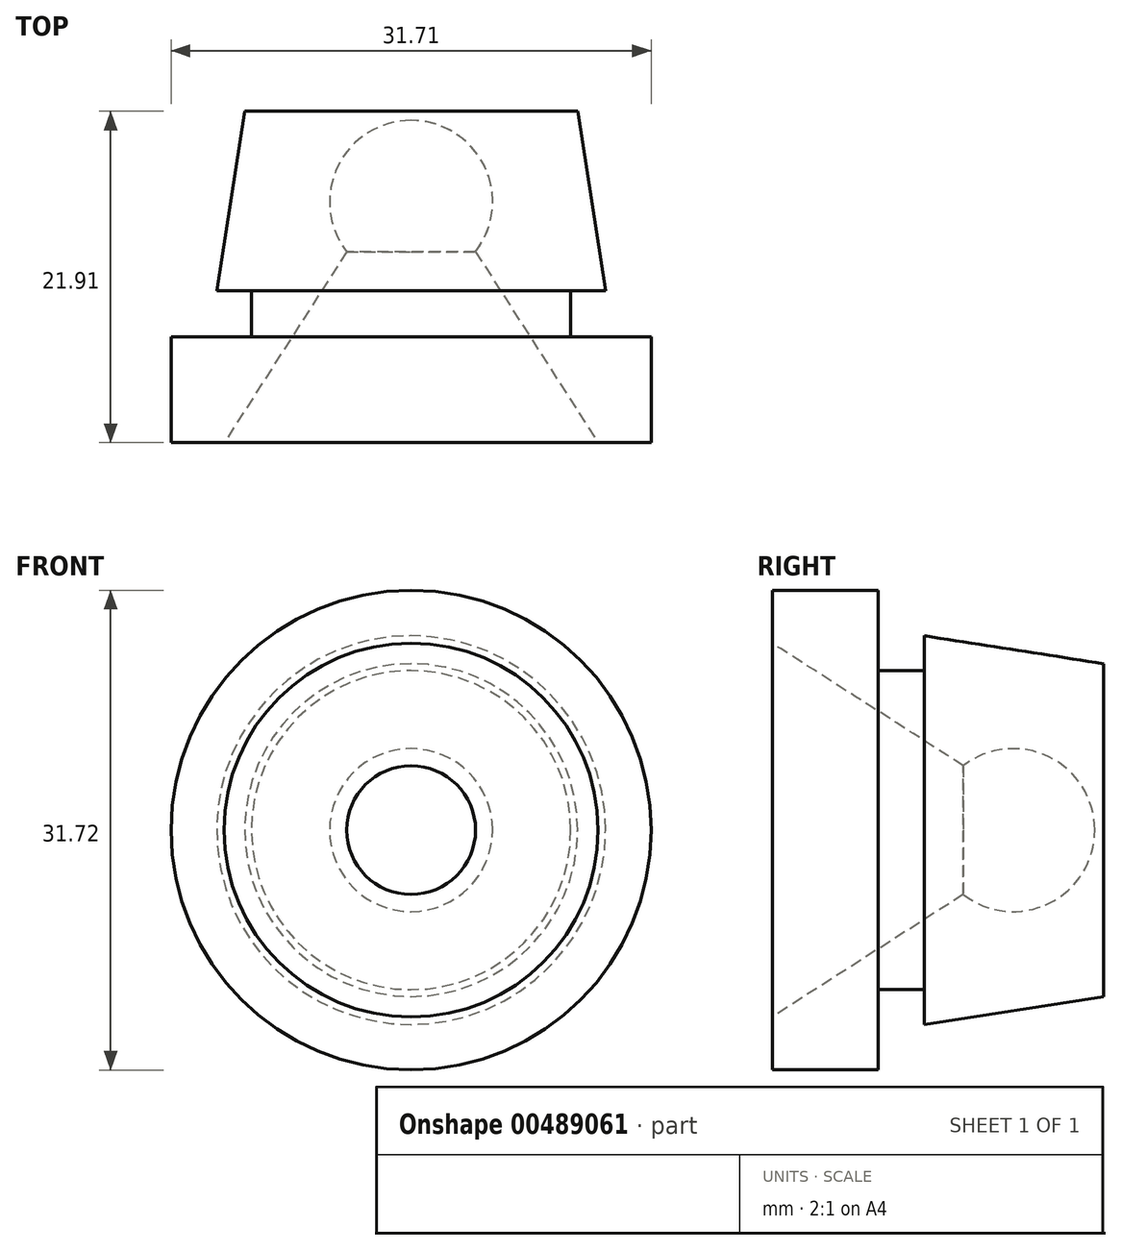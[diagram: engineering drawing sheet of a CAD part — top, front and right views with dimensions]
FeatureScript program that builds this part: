
annotation { "Feature Type Name" : "Feature", "Feature Type Description" : "" }
export const myFeature = defineFeature(function(context is Context, id is Id, definition is map)
    precondition{}
    {
        {
            var Q0;
            Q0=qCreatedBy(makeId("Top.planeOp"),FACE);
            var sketch = newSketch(context, id + "F0", { "sketchPlane" : qUnion([Q0])});
            skLineSegment(sketch, "E0", {"start": v(0, 0) * mm, "end": v(3.5, 0) * mm});
            skLineSegment(sketch, "E1", {"start": v(3.5, 0) * mm, "end": v(3.5, 7) * mm});
            skLineSegment(sketch, "E2", {"start": v(3.5, 7) * mm, "end": v(-1.81, 7) * mm});
            skLineSegment(sketch, "E3", {"start": v(-1.81, 7) * mm, "end": v(-1.81, 10.05) * mm});
            skLineSegment(sketch, "E4", {"start": v(-1.81, 10.05) * mm, "end": v(0.5, 10.05) * mm});
            skLineSegment(sketch, "E5", {"start": v(0.5, 10.05) * mm, "end": v(-1.36, 21.9) * mm});
            skLineSegment(sketch, "E6", {"start": v(-1.36, 21.9) * mm, "end": v(-12.36, 21.9) * mm});
            skLineSegment(sketch, "E7", {"start": v(0, 0) * mm, "end": v(-8.1, 12.62) * mm});
            skArc(sketch, "E8", {"start": v(-8.1, 12.62) * mm, "mid": v(-7.52, 18.3) * mm, "end": v(-12.36, 21.3) * mm});
            skLineSegment(sketch, "E9", {"start": v(-12.36, 21.9) * mm, "end": v(-12.36, 0) * mm, "construction": true});
            skLineSegment(sketch, "E10", {"start": v(-12.36, 0) * mm, "end": v(0, 0) * mm, "construction": true});
            skLineSegment(sketch, "E11", {"start": v(-12.36, 21.9) * mm, "end": v(-12.36, 21.3) * mm});
            skSolve(sketch);
        }
        {
            var Q0;
            Q0 = qSketchRegion(id + "F0", true);
            var Q1;
            Q1=sQuery(id+"F0.wireOp",EDGE,"E9");
            revolve(context, id + "F1", {"entities" : qUnion([Q0]), "axis" : qUnion([Q1]), "revolveType" : RevolveType.FULL});
        }
    });
